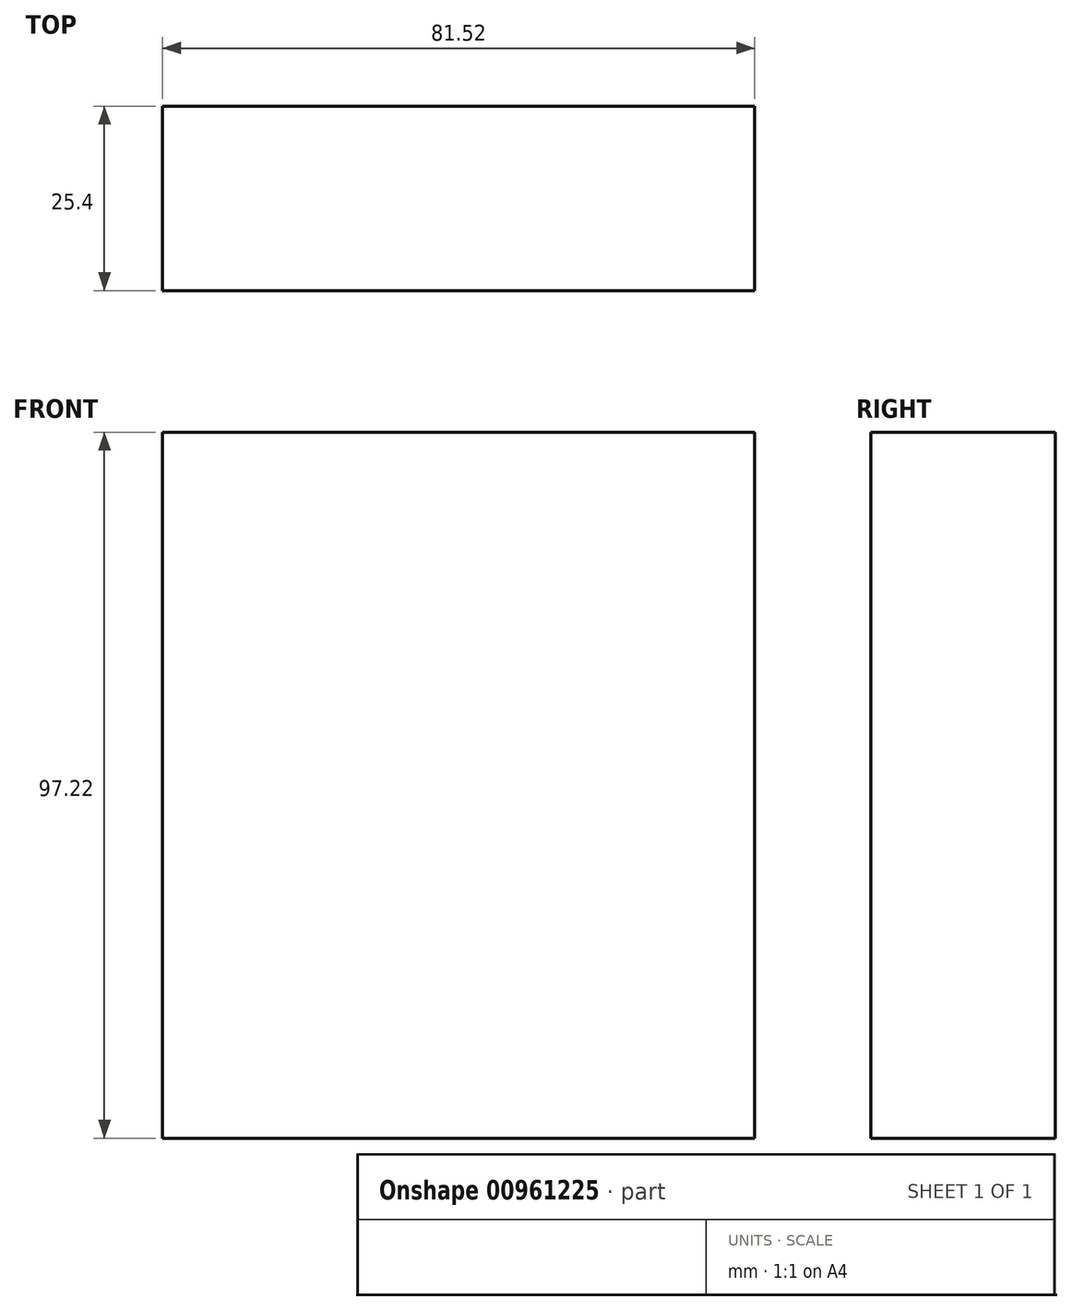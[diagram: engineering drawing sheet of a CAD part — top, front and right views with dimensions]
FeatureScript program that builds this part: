
annotation { "Feature Type Name" : "Feature", "Feature Type Description" : "" }
export const myFeature = defineFeature(function(context is Context, id is Id, definition is map)
    precondition{}
    {
        {
            var Q0;
            Q0=qCreatedBy(makeId("Front.planeOp"),FACE);
            var sketch = newSketch(context, id + "F0", { "sketchPlane" : qUnion([Q0])});
            skLineSegment(sketch, "E0.bottom", {"start": v(-44.2, 50.26) * mm, "end": v(37.32, 50.26) * mm});
            skLineSegment(sketch, "E0.top", {"start": v(-44.2, -46.96) * mm, "end": v(37.32, -46.96) * mm});
            skLineSegment(sketch, "E0.left", {"start": v(-44.2, 50.26) * mm, "end": v(-44.2, -46.96) * mm});
            skLineSegment(sketch, "E0.right", {"start": v(37.32, 50.26) * mm, "end": v(37.32, -46.96) * mm});
            skSolve(sketch);
        }
        {
            var Q0;
            Q0 = qSketchRegion(id + "F0", true);
            extrude(context, id + "F1", {"entities" : qUnion([Q0]), "depth" : 25.4 * mm, "offsetDistance" : 25.4 * mm});
        }
    });
